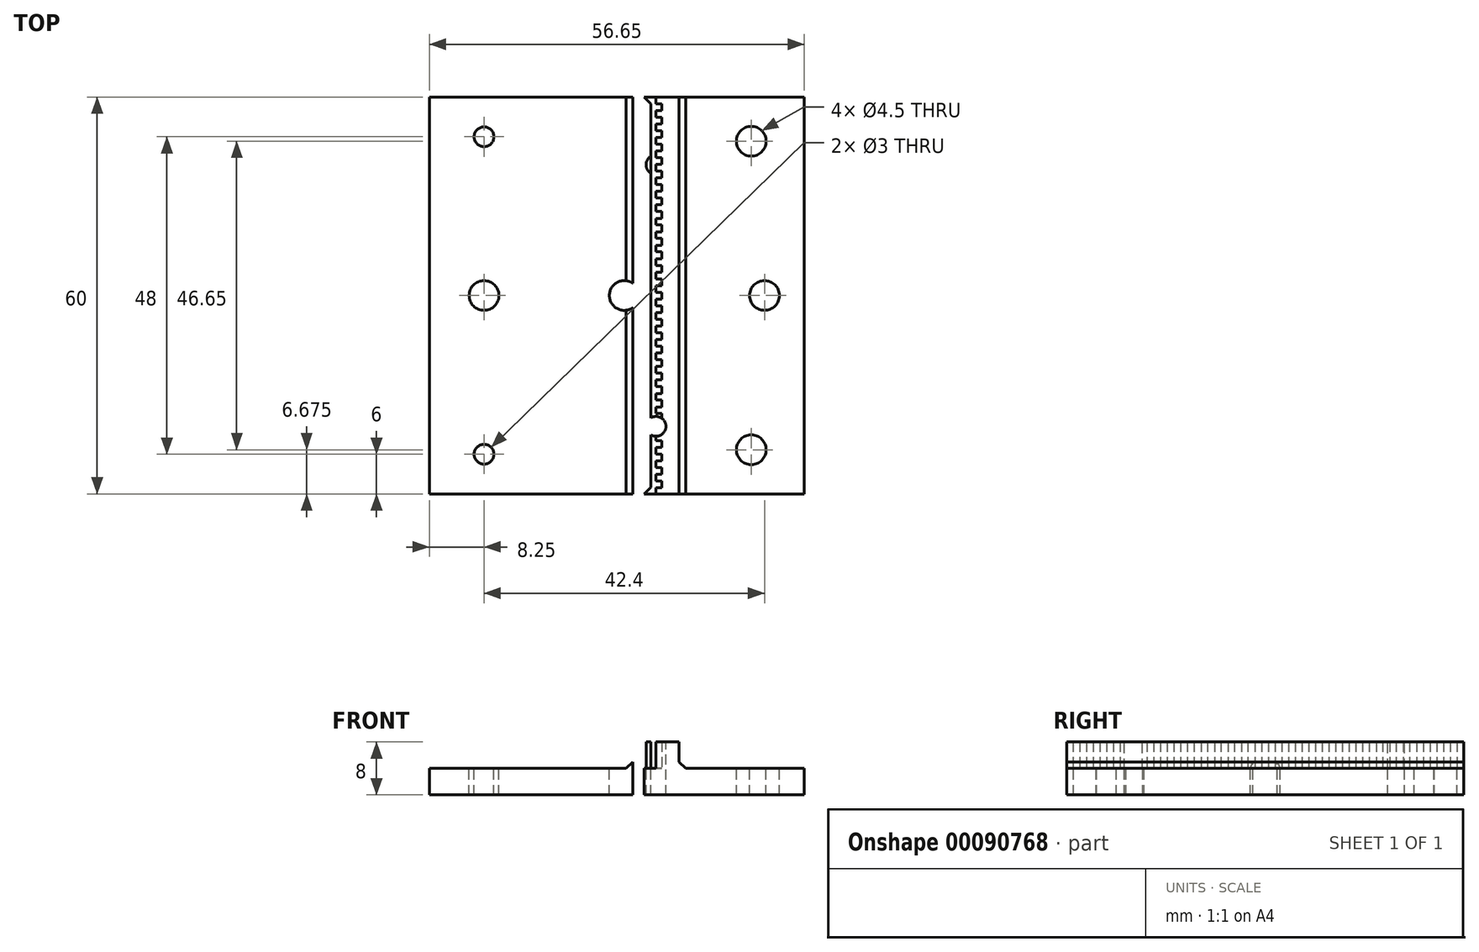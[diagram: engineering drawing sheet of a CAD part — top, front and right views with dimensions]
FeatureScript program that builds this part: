
annotation { "Feature Type Name" : "Feature", "Feature Type Description" : "" }
export const myFeature = defineFeature(function(context is Context, id is Id, definition is map)
    precondition{}
    {
        {
            var Q0;
            Q0=qCreatedBy(makeId("Top.planeOp"),FACE);
            var sketch = newSketch(context, id + "F0", { "sketchPlane" : qUnion([Q0])});
            skLineSegment(sketch, "E0.bottom", {"start": v(28.2, 30) * mm, "end": v(-63.8, 30) * mm});
            skLineSegment(sketch, "E0.top", {"start": v(28.2, -30) * mm, "end": v(-63.8, -30) * mm});
            skLineSegment(sketch, "E0.left", {"start": v(28.2, 30) * mm, "end": v(28.2, -30) * mm});
            skLineSegment(sketch, "E0.right", {"start": v(-63.8, 30) * mm, "end": v(-63.8, -30) * mm});
            skPoint(sketch, "E0.middle", {"position": v(-17.8, 0) * mm});
            skCircle(sketch, "E1.cCircle", {"center": v(6.73, 0) * mm, "radius": 13.47 * mm, "construction": true});
            skLineSegment(sketch, "E1.0", {"start": v(20.2, 23.32) * mm, "end": v(20.2, -23.32) * mm, "construction": true});
            skLineSegment(sketch, "E1.1", {"start": v(20.2, -23.32) * mm, "end": v(-20.2, 0) * mm, "construction": true});
            skLineSegment(sketch, "E1.2", {"start": v(-20.2, 0) * mm, "end": v(20.2, 23.32) * mm, "construction": true});
            skPoint(sketch, "E1.0.midPoint", {"position": v(20.2, 0) * mm});
            skLineSegment(sketch, "E2", {"start": v(-12.7, 30) * mm, "end": v(-12.7, -30) * mm, "construction": true});
            skLineSegment(sketch, "E3", {"start": v(12.7, 30) * mm, "end": v(12.7, -30) * mm, "construction": true});
            skCircle(sketch, "E4", {"center": v(-20.2, 0) * mm, "radius": 2.25 * mm});
            skCircle(sketch, "E5.1.0", {"center": v(20.2, -23.32) * mm, "radius": 2.25 * mm});
            skCircle(sketch, "E5.2.0", {"center": v(20.2, 23.32) * mm, "radius": 2.25 * mm});
            skCircle(sketch, "E6", {"center": v(22.2, 0) * mm, "radius": 2.25 * mm});
            skLineSegment(sketch, "E7.bottom", {"start": v(-33.95, 13) * mm, "end": v(-59.95, 13) * mm, "construction": true});
            skLineSegment(sketch, "E7.top", {"start": v(-33.95, -13) * mm, "end": v(-59.95, -13) * mm, "construction": true});
            skLineSegment(sketch, "E7.left", {"start": v(-33.95, 13) * mm, "end": v(-33.95, -13) * mm, "construction": true});
            skLineSegment(sketch, "E7.right", {"start": v(-59.95, 13) * mm, "end": v(-59.95, -13) * mm, "construction": true});
            skPoint(sketch, "E7.middle", {"position": v(-46.95, 0) * mm});
            skLineSegment(sketch, "E8", {"start": v(-12.7, 0) * mm, "end": v(12.7, 0) * mm, "construction": true});
            skCircle(sketch, "E9", {"center": v(-59.95, 13) * mm, "radius": 1.5 * mm});
            skCircle(sketch, "E10.1.0", {"center": v(-59.95, -13) * mm, "radius": 1.5 * mm});
            skCircle(sketch, "E10.2.0", {"center": v(-33.95, -13) * mm, "radius": 1.5 * mm});
            skCircle(sketch, "E10.3.0", {"center": v(-33.95, 13) * mm, "radius": 1.5 * mm});
            skLineSegment(sketch, "E11.0", {"start": v(-64, 30.2) * mm, "end": v(-64, -30.2) * mm});
            skLineSegment(sketch, "E11.1", {"start": v(28.4, 30.2) * mm, "end": v(-64, 30.2) * mm});
            skLineSegment(sketch, "E11.2", {"start": v(28.4, 30.2) * mm, "end": v(28.4, -30.2) * mm});
            skLineSegment(sketch, "E11.3", {"start": v(28.4, -30.2) * mm, "end": v(-64, -30.2) * mm});
            skLineSegment(sketch, "E12", {"start": v(-28.45, -30.2) * mm, "end": v(-28.45, 30.2) * mm});
            skCircle(sketch, "E13", {"center": v(1, 0) * mm, "radius": 2.25 * mm});
            skCircle(sketch, "E14", {"center": v(-20.2, 24) * mm, "radius": 1.5 * mm});
            skCircle(sketch, "E15.MirrorC", {"center": v(-20.2, -24) * mm, "radius": 1.5 * mm});
            skSolve(sketch);
        }
        {
            var Q0;
            {var subQ0=sQuery(id+"F0.wireOp",EDGE,"E0.left");Q0=makeQuery(id+"F0.imprint","IMPRINT",FACE,{"disambiguationData":[TD([[makeQuery(id+"F0.imprint","IMPRINT",EDGE,{"derivedFrom":subQ0}),-1.0]])]});}
            extrude(context, id + "F1", {"entities" : qUnion([Q0]), "oppositeDirection" : true, "depth" : 1 * mm});
        }
        {
            var Q0;
            {var subQ0=sQuery(id+"F0.wireOp",EDGE,"E0.left");Q0=makeQuery(id+"F0.imprint","IMPRINT",FACE,{"disambiguationData":[TD([[makeQuery(id+"F0.imprint","IMPRINT",EDGE,{"derivedFrom":subQ0}),-1.0]])]});}
            extrude(context, id + "F2", {"entities" : qUnion([Q0]), "operationType" : NewBodyOperationType.ADD, "depth" : 3 * mm});
        }
        {
            var Q0;
            Q0=makeQuery(id+"F2.opExtrude","CAP_FACE",FACE,{"disambiguationData":[OSD([sQuery(id+"F0.wireOp",EDGE,"E0.bottom"),sQuery(id+"F0.wireOp",EDGE,"E0.top"),sQuery(id+"F0.wireOp",EDGE,"E0.left"),sQuery(id+"F0.wireOp",EDGE,"E0.right"),sQuery(id+"F0.wireOp",EDGE,"E4"),sQuery(id+"F0.wireOp",EDGE,"E5.1.0"),sQuery(id+"F0.wireOp",EDGE,"E5.2.0"),sQuery(id+"F0.wireOp",EDGE,"E6"),sQuery(id+"F0.wireOp",EDGE,"E9"),sQuery(id+"F0.wireOp",EDGE,"E10.1.0"),sQuery(id+"F0.wireOp",EDGE,"E10.2.0"),sQuery(id+"F0.wireOp",EDGE,"E10.3.0")])],"isStart":false});
            var sketch = newSketch(context, id + "F3", { "sketchPlane" : qUnion([Q0])});
            skLineSegment(sketch, "E16", {"start": v(5.8, 30) * mm, "end": v(5.8, 29) * mm});
            skLineSegment(sketch, "E17", {"start": v(5.8, 29) * mm, "end": v(6.7, 29) * mm});
            skLineSegment(sketch, "E18", {"start": v(6.7, 29) * mm, "end": v(6.7, 27.96) * mm});
            skLineSegment(sketch, "E19", {"start": v(5.8, 30) * mm, "end": v(6.7, 30) * mm});
            skLineSegment(sketch, "E20.0.1.0", {"start": v(5.8, 27.96) * mm, "end": v(6.7, 27.96) * mm});
            skLineSegment(sketch, "E20.0.1.1", {"start": v(5.8, 27.96) * mm, "end": v(5.8, 26.96) * mm});
            skLineSegment(sketch, "E20.0.1.2", {"start": v(5.8, 26.96) * mm, "end": v(6.7, 26.96) * mm});
            skLineSegment(sketch, "E20.0.1.3", {"start": v(6.7, 26.96) * mm, "end": v(6.7, 25.93) * mm});
            skLineSegment(sketch, "E20.0.2.0", {"start": v(5.8, 25.93) * mm, "end": v(6.7, 25.93) * mm});
            skLineSegment(sketch, "E20.0.2.1", {"start": v(5.8, 25.93) * mm, "end": v(5.8, 24.93) * mm});
            skLineSegment(sketch, "E20.0.2.2", {"start": v(5.8, 24.93) * mm, "end": v(6.7, 24.93) * mm});
            skLineSegment(sketch, "E20.0.2.3", {"start": v(6.7, 24.93) * mm, "end": v(6.7, 23.89) * mm});
            skLineSegment(sketch, "E20.0.3.0", {"start": v(5.8, 23.89) * mm, "end": v(6.7, 23.89) * mm});
            skLineSegment(sketch, "E20.0.3.1", {"start": v(5.8, 23.89) * mm, "end": v(5.8, 22.89) * mm});
            skLineSegment(sketch, "E20.0.3.2", {"start": v(5.8, 22.89) * mm, "end": v(6.7, 22.89) * mm});
            skLineSegment(sketch, "E20.0.3.3", {"start": v(6.7, 22.89) * mm, "end": v(6.7, 21.85) * mm});
            skLineSegment(sketch, "E20.0.4.0", {"start": v(5.8, 21.85) * mm, "end": v(6.7, 21.85) * mm});
            skLineSegment(sketch, "E20.0.4.1", {"start": v(5.8, 21.85) * mm, "end": v(5.8, 20.85) * mm});
            skLineSegment(sketch, "E20.0.4.2", {"start": v(5.8, 20.85) * mm, "end": v(6.7, 20.85) * mm});
            skLineSegment(sketch, "E20.0.4.3", {"start": v(6.7, 20.85) * mm, "end": v(6.7, 19.82) * mm});
            skLineSegment(sketch, "E20.0.5.0", {"start": v(5.8, 19.82) * mm, "end": v(6.7, 19.82) * mm});
            skLineSegment(sketch, "E20.0.5.1", {"start": v(5.8, 19.82) * mm, "end": v(5.8, 18.82) * mm});
            skLineSegment(sketch, "E20.0.5.2", {"start": v(5.8, 18.82) * mm, "end": v(6.7, 18.82) * mm});
            skLineSegment(sketch, "E20.0.5.3", {"start": v(6.7, 18.82) * mm, "end": v(6.7, 17.78) * mm});
            skLineSegment(sketch, "E20.0.6.0", {"start": v(5.8, 17.78) * mm, "end": v(6.7, 17.78) * mm});
            skLineSegment(sketch, "E20.0.6.1", {"start": v(5.8, 17.78) * mm, "end": v(5.8, 16.78) * mm});
            skLineSegment(sketch, "E20.0.6.2", {"start": v(5.8, 16.78) * mm, "end": v(6.7, 16.78) * mm});
            skLineSegment(sketch, "E20.0.6.3", {"start": v(6.7, 16.78) * mm, "end": v(6.7, 15.74) * mm});
            skLineSegment(sketch, "E20.0.7.0", {"start": v(5.8, 15.74) * mm, "end": v(6.7, 15.74) * mm});
            skLineSegment(sketch, "E20.0.7.1", {"start": v(5.8, 15.74) * mm, "end": v(5.8, 14.74) * mm});
            skLineSegment(sketch, "E20.0.7.2", {"start": v(5.8, 14.74) * mm, "end": v(6.7, 14.74) * mm});
            skLineSegment(sketch, "E20.0.7.3", {"start": v(6.7, 14.74) * mm, "end": v(6.7, 13.7) * mm});
            skLineSegment(sketch, "E20.0.8.0", {"start": v(5.8, 13.7) * mm, "end": v(6.7, 13.7) * mm});
            skLineSegment(sketch, "E20.0.8.1", {"start": v(5.8, 13.7) * mm, "end": v(5.8, 12.7) * mm});
            skLineSegment(sketch, "E20.0.8.2", {"start": v(5.8, 12.7) * mm, "end": v(6.7, 12.7) * mm});
            skLineSegment(sketch, "E20.0.8.3", {"start": v(6.7, 12.7) * mm, "end": v(6.7, 11.67) * mm});
            skLineSegment(sketch, "E20.0.9.0", {"start": v(5.8, 11.67) * mm, "end": v(6.7, 11.67) * mm});
            skLineSegment(sketch, "E20.0.9.1", {"start": v(5.8, 11.67) * mm, "end": v(5.8, 10.67) * mm});
            skLineSegment(sketch, "E20.0.9.2", {"start": v(5.8, 10.67) * mm, "end": v(6.7, 10.67) * mm});
            skLineSegment(sketch, "E20.0.9.3", {"start": v(6.7, 10.67) * mm, "end": v(6.7, 9.63) * mm});
            skLineSegment(sketch, "E20.0.10.0", {"start": v(5.8, 9.63) * mm, "end": v(6.7, 9.63) * mm});
            skLineSegment(sketch, "E20.0.10.1", {"start": v(5.8, 9.63) * mm, "end": v(5.8, 8.63) * mm});
            skLineSegment(sketch, "E20.0.10.2", {"start": v(5.8, 8.63) * mm, "end": v(6.7, 8.63) * mm});
            skLineSegment(sketch, "E20.0.10.3", {"start": v(6.7, 8.63) * mm, "end": v(6.7, 7.6) * mm});
            skLineSegment(sketch, "E20.0.11.0", {"start": v(5.8, 7.6) * mm, "end": v(6.7, 7.6) * mm});
            skLineSegment(sketch, "E20.0.11.1", {"start": v(5.8, 7.6) * mm, "end": v(5.8, 6.6) * mm});
            skLineSegment(sketch, "E20.0.11.2", {"start": v(5.8, 6.6) * mm, "end": v(6.7, 6.6) * mm});
            skLineSegment(sketch, "E20.0.11.3", {"start": v(6.7, 6.6) * mm, "end": v(6.7, 5.56) * mm});
            skLineSegment(sketch, "E20.0.12.0", {"start": v(5.8, 5.56) * mm, "end": v(6.7, 5.56) * mm});
            skLineSegment(sketch, "E20.0.12.1", {"start": v(5.8, 5.56) * mm, "end": v(5.8, 4.56) * mm});
            skLineSegment(sketch, "E20.0.12.2", {"start": v(5.8, 4.56) * mm, "end": v(6.7, 4.56) * mm});
            skLineSegment(sketch, "E20.0.12.3", {"start": v(6.7, 4.56) * mm, "end": v(6.7, 3.52) * mm});
            skLineSegment(sketch, "E20.0.13.0", {"start": v(5.8, 3.52) * mm, "end": v(6.7, 3.52) * mm});
            skLineSegment(sketch, "E20.0.13.1", {"start": v(5.8, 3.52) * mm, "end": v(5.8, 2.52) * mm});
            skLineSegment(sketch, "E20.0.13.2", {"start": v(5.8, 2.52) * mm, "end": v(6.7, 2.52) * mm});
            skLineSegment(sketch, "E20.0.13.3", {"start": v(6.7, 2.52) * mm, "end": v(6.7, 1.48) * mm});
            skLineSegment(sketch, "E20.0.14.0", {"start": v(5.8, 1.48) * mm, "end": v(6.7, 1.48) * mm});
            skLineSegment(sketch, "E20.0.14.1", {"start": v(5.8, 1.48) * mm, "end": v(5.8, 0.48) * mm});
            skLineSegment(sketch, "E20.0.14.2", {"start": v(5.8, 0.48) * mm, "end": v(6.7, 0.48) * mm});
            skLineSegment(sketch, "E20.0.14.3", {"start": v(6.7, 0.48) * mm, "end": v(6.7, -0.55) * mm});
            skLineSegment(sketch, "E20.0.15.0", {"start": v(5.8, -0.55) * mm, "end": v(6.7, -0.55) * mm});
            skLineSegment(sketch, "E20.0.15.1", {"start": v(5.8, -0.55) * mm, "end": v(5.8, -1.55) * mm});
            skLineSegment(sketch, "E20.0.15.2", {"start": v(5.8, -1.55) * mm, "end": v(6.7, -1.55) * mm});
            skLineSegment(sketch, "E20.0.15.3", {"start": v(6.7, -1.55) * mm, "end": v(6.7, -2.6) * mm});
            skLineSegment(sketch, "E20.0.16.0", {"start": v(5.8, -2.6) * mm, "end": v(6.7, -2.6) * mm});
            skLineSegment(sketch, "E20.0.16.1", {"start": v(5.8, -2.6) * mm, "end": v(5.8, -3.6) * mm});
            skLineSegment(sketch, "E20.0.16.2", {"start": v(5.8, -3.6) * mm, "end": v(6.7, -3.6) * mm});
            skLineSegment(sketch, "E20.0.16.3", {"start": v(6.7, -3.6) * mm, "end": v(6.7, -4.63) * mm});
            skLineSegment(sketch, "E20.0.17.0", {"start": v(5.8, -4.63) * mm, "end": v(6.7, -4.63) * mm});
            skLineSegment(sketch, "E20.0.17.1", {"start": v(5.8, -4.63) * mm, "end": v(5.8, -5.63) * mm});
            skLineSegment(sketch, "E20.0.17.2", {"start": v(5.8, -5.63) * mm, "end": v(6.7, -5.63) * mm});
            skLineSegment(sketch, "E20.0.17.3", {"start": v(6.7, -5.63) * mm, "end": v(6.7, -6.67) * mm});
            skLineSegment(sketch, "E20.0.18.0", {"start": v(5.8, -6.67) * mm, "end": v(6.7, -6.67) * mm});
            skLineSegment(sketch, "E20.0.18.1", {"start": v(5.8, -6.67) * mm, "end": v(5.8, -7.67) * mm});
            skLineSegment(sketch, "E20.0.18.2", {"start": v(5.8, -7.67) * mm, "end": v(6.7, -7.67) * mm});
            skLineSegment(sketch, "E20.0.18.3", {"start": v(6.7, -7.67) * mm, "end": v(6.7, -8.7) * mm});
            skLineSegment(sketch, "E20.0.19.0", {"start": v(5.8, -8.7) * mm, "end": v(6.7, -8.7) * mm});
            skLineSegment(sketch, "E20.0.19.1", {"start": v(5.8, -8.7) * mm, "end": v(5.8, -9.7) * mm});
            skLineSegment(sketch, "E20.0.19.2", {"start": v(5.8, -9.7) * mm, "end": v(6.7, -9.7) * mm});
            skLineSegment(sketch, "E20.0.19.3", {"start": v(6.7, -9.7) * mm, "end": v(6.7, -10.74) * mm});
            skLineSegment(sketch, "E20.0.20.0", {"start": v(5.8, -10.74) * mm, "end": v(6.7, -10.74) * mm});
            skLineSegment(sketch, "E20.0.20.1", {"start": v(5.8, -10.74) * mm, "end": v(5.8, -11.74) * mm});
            skLineSegment(sketch, "E20.0.20.2", {"start": v(5.8, -11.74) * mm, "end": v(6.7, -11.74) * mm});
            skLineSegment(sketch, "E20.0.20.3", {"start": v(6.7, -11.74) * mm, "end": v(6.7, -12.78) * mm});
            skLineSegment(sketch, "E20.0.21.0", {"start": v(5.8, -12.78) * mm, "end": v(6.7, -12.78) * mm});
            skLineSegment(sketch, "E20.0.21.1", {"start": v(5.8, -12.78) * mm, "end": v(5.8, -13.78) * mm});
            skLineSegment(sketch, "E20.0.21.2", {"start": v(5.8, -13.78) * mm, "end": v(6.7, -13.78) * mm});
            skLineSegment(sketch, "E20.0.21.3", {"start": v(6.7, -13.78) * mm, "end": v(6.7, -14.81) * mm});
            skLineSegment(sketch, "E20.0.22.0", {"start": v(5.8, -14.81) * mm, "end": v(6.7, -14.81) * mm});
            skLineSegment(sketch, "E20.0.22.1", {"start": v(5.8, -14.81) * mm, "end": v(5.8, -15.81) * mm});
            skLineSegment(sketch, "E20.0.22.2", {"start": v(5.8, -15.81) * mm, "end": v(6.7, -15.81) * mm});
            skLineSegment(sketch, "E20.0.22.3", {"start": v(6.7, -15.81) * mm, "end": v(6.7, -16.85) * mm});
            skLineSegment(sketch, "E20.0.23.0", {"start": v(5.8, -16.85) * mm, "end": v(6.7, -16.85) * mm});
            skLineSegment(sketch, "E20.0.23.1", {"start": v(5.8, -16.85) * mm, "end": v(5.8, -17.85) * mm});
            skLineSegment(sketch, "E20.0.23.2", {"start": v(5.8, -17.85) * mm, "end": v(6.7, -17.85) * mm});
            skLineSegment(sketch, "E20.0.23.3", {"start": v(6.7, -17.85) * mm, "end": v(6.7, -18.89) * mm});
            skLineSegment(sketch, "E20.0.24.0", {"start": v(5.8, -18.89) * mm, "end": v(6.7, -18.89) * mm});
            skLineSegment(sketch, "E20.0.24.1", {"start": v(5.8, -18.89) * mm, "end": v(5.8, -19.89) * mm});
            skLineSegment(sketch, "E20.0.24.2", {"start": v(5.8, -19.89) * mm, "end": v(6.7, -19.89) * mm});
            skLineSegment(sketch, "E20.0.24.3", {"start": v(6.7, -19.89) * mm, "end": v(6.7, -20.92) * mm});
            skLineSegment(sketch, "E20.0.25.0", {"start": v(5.8, -20.92) * mm, "end": v(6.7, -20.92) * mm});
            skLineSegment(sketch, "E20.0.25.1", {"start": v(5.8, -20.92) * mm, "end": v(5.8, -21.92) * mm});
            skLineSegment(sketch, "E20.0.25.2", {"start": v(5.8, -21.92) * mm, "end": v(6.7, -21.92) * mm});
            skLineSegment(sketch, "E20.0.25.3", {"start": v(6.7, -21.92) * mm, "end": v(6.7, -22.96) * mm});
            skLineSegment(sketch, "E20.0.26.0", {"start": v(5.8, -22.96) * mm, "end": v(6.7, -22.96) * mm});
            skLineSegment(sketch, "E20.0.26.1", {"start": v(5.8, -22.96) * mm, "end": v(5.8, -23.96) * mm});
            skLineSegment(sketch, "E20.0.26.2", {"start": v(5.8, -23.96) * mm, "end": v(6.7, -23.96) * mm});
            skLineSegment(sketch, "E20.0.26.3", {"start": v(6.7, -23.96) * mm, "end": v(6.7, -25) * mm});
            skLineSegment(sketch, "E20.0.27.0", {"start": v(5.8, -25) * mm, "end": v(6.7, -25) * mm});
            skLineSegment(sketch, "E20.0.27.1", {"start": v(5.8, -25) * mm, "end": v(5.8, -26) * mm});
            skLineSegment(sketch, "E20.0.27.2", {"start": v(5.8, -26) * mm, "end": v(6.7, -26) * mm});
            skLineSegment(sketch, "E20.0.27.3", {"start": v(6.7, -26) * mm, "end": v(6.7, -27.04) * mm});
            skLineSegment(sketch, "E20.0.28.0", {"start": v(5.8, -27.04) * mm, "end": v(6.7, -27.04) * mm});
            skLineSegment(sketch, "E20.0.28.1", {"start": v(5.8, -27.04) * mm, "end": v(5.8, -28.04) * mm});
            skLineSegment(sketch, "E20.0.28.2", {"start": v(5.8, -28.04) * mm, "end": v(6.7, -28.04) * mm});
            skLineSegment(sketch, "E20.0.28.3", {"start": v(6.7, -28.04) * mm, "end": v(6.7, -29.07) * mm});
            skLineSegment(sketch, "E20.direction1", {"start": v(5.8, 30) * mm, "end": v(27.82, 30) * mm, "construction": true});
            skLineSegment(sketch, "E20.direction2", {"start": v(5.8, 30) * mm, "end": v(5.8, 27.96) * mm, "construction": true});
            skLineSegment(sketch, "E21.0.0.29", {"start": v(5.8, -29.07) * mm, "end": v(6.7, -29.07) * mm});
            skLineSegment(sketch, "E21.3.0.29", {"start": v(5.8, -29.07) * mm, "end": v(5.8, -30.07) * mm});
            skLineSegment(sketch, "E21.6.0.29", {"start": v(5.8, -30.07) * mm, "end": v(6.7, -30.07) * mm});
            skLineSegment(sketch, "E21.9.0.29", {"start": v(6.7, -30.07) * mm, "end": v(6.7, -31.1) * mm});
            skLineSegment(sketch, "E22", {"start": v(2.3, 30) * mm, "end": v(2.3, -30) * mm});
            skLineSegment(sketch, "E23", {"start": v(9.3, -30) * mm, "end": v(9.3, 30) * mm});
            skLineSegment(sketch, "E24", {"start": v(5, -30) * mm, "end": v(5, 30) * mm});
            skSolve(sketch);
        }
        {
            var Q0;
            {var subQ0=sQuery(id+"F3.wireOp",EDGE,"E22");Q0=makeQuery(id+"F3.imprint","IMPRINT",FACE,{"disambiguationData":[TD([[makeQuery(id+"F3.imprint","IMPRINT",EDGE,{"derivedFrom":subQ0}),1.0]])]});}
            var Q1;
            Q1=makeQuery(id+"F3.imprint","IMPRINT",FACE,{"disambiguationData":[TD([[makeQuery(id+"F3.imprint","IMPRINT",EDGE,{"derivedFrom":sQuery(id+"F3.wireOp",EDGE,"E16")}),1.0]])]});
            extrude(context, id + "F4", {"entities" : qUnion([Q0, Q1]), "operationType" : NewBodyOperationType.ADD, "depth" : 4 * mm});
        }
        {
            var Q0;
            Q0=makeQuery(id+"F4.opExtrude","CAP_EDGE",EDGE,{"disambiguationData":[OSD([sQuery(id+"F3.wireOp",EDGE,"E22")])],"isStart":true});
            var Q1;
            Q1=makeQuery(id+"F4.opExtrude","CAP_EDGE",EDGE,{"disambiguationData":[OSD([sQuery(id+"F3.wireOp",EDGE,"E23")])],"isStart":true});
            var Q2;
            Q2=makeQuery(id+"F4.opExtrude","SWEPT_EDGE",EDGE,{"disambiguationData":[OSD([sQuery(id+"F0.wireOp",EDGE,"E0.top"),sQuery(id+"F3.wireOp",EDGE,"E24")])]});
            var Q3;
            Q3=makeQuery(id+"F4.opExtrude","SWEPT_EDGE",EDGE,{"disambiguationData":[OSD([sQuery(id+"F0.wireOp",EDGE,"E0.bottom"),sQuery(id+"F3.wireOp",EDGE,"E24")])]});
            chamfer(context, id + "F5", {"entities" : qUnion([Q0, Q1, Q2, Q3]), "width" : 1 * mm, "tangentPropagation" : true});
        }
        {
            var Q0;
            Q0=makeQuery(id+"F4.opExtrude","CAP_FACE",FACE,{"disambiguationData":[OSD([sQuery(id+"F0.wireOp",EDGE,"E0.bottom"),sQuery(id+"F0.wireOp",EDGE,"E0.top"),sQuery(id+"F3.wireOp",EDGE,"E22"),sQuery(id+"F3.wireOp",EDGE,"E24")])],"isStart":false});
            var sketch = newSketch(context, id + "F6", { "sketchPlane" : qUnion([Q0])});
            skLineSegment(sketch, "E25", {"start": v(2.3, 0) * mm, "end": v(9.3, 0) * mm, "construction": true});
            skCircle(sketch, "E26", {"center": v(5.8, -19.78) * mm, "radius": 1.5 * mm});
            skLineSegment(sketch, "E27.0", {"start": v(9.3, -30) * mm, "end": v(9.3, 30) * mm});
            skPoint(sketch, "E28", {"position": v(5.8, 0) * mm});
            skCircle(sketch, "E29.MirrorC", {"center": v(5.8, 19.78) * mm, "radius": 1.5 * mm});
            skSolve(sketch);
        }
        {
            var Q0;
            {var subQ0=sQuery(id+"F6.wireOp",EDGE,"E26");var subQ1=makeQuery(id+"F4.opExtrude","CAP_EDGE",EDGE,{"disambiguationData":[OSD([sQuery(id+"F3.wireOp",EDGE,"E24")])],"isStart":false});var subQ2=makeQuery(id+"F6.imprint","INTERSECT",VERTEX,{"disambiguationData":[OD(0.0)],"derivedFrom":[subQ1,subQ0]});Q0=makeQuery(id+"F6.imprint","IMPRINT",FACE,{"disambiguationData":[TD([[makeQuery(id+"F6.imprint","IMPRINT",EDGE,{"disambiguationData":[TD([[subQ2,-1.0]])],"derivedFrom":subQ0}),1.0]])]});}
            var Q1;
            {var subQ0=sQuery(id+"F6.wireOp",EDGE,"E26");var subQ1=makeQuery(id+"F4.opExtrude","CAP_EDGE",EDGE,{"disambiguationData":[OSD([sQuery(id+"F3.wireOp",EDGE,"E24")])],"isStart":false});var subQ2=makeQuery(id+"F6.imprint","INTERSECT",VERTEX,{"disambiguationData":[OD(0.0)],"derivedFrom":[subQ1,subQ0]});Q1=makeQuery(id+"F6.imprint","IMPRINT",FACE,{"disambiguationData":[TD([[makeQuery(id+"F6.imprint","IMPRINT",EDGE,{"disambiguationData":[TD([[subQ2,1.0]])],"derivedFrom":subQ0}),1.0]])]});}
            var Q2;
            {var subQ0=sQuery(id+"F6.wireOp",EDGE,"E29.MirrorC");var subQ1=makeQuery(id+"F4.opExtrude","CAP_EDGE",EDGE,{"disambiguationData":[OSD([sQuery(id+"F3.wireOp",EDGE,"E24")])],"isStart":false});var subQ2=makeQuery(id+"F6.imprint","INTERSECT",VERTEX,{"disambiguationData":[OD(0.0)],"derivedFrom":[subQ1,subQ0]});Q2=makeQuery(id+"F6.imprint","IMPRINT",FACE,{"disambiguationData":[TD([[makeQuery(id+"F6.imprint","IMPRINT",EDGE,{"disambiguationData":[TD([[subQ2,1.0]])],"derivedFrom":subQ0}),-1.0]])]});}
            var Q3;
            {var subQ0=sQuery(id+"F6.wireOp",EDGE,"E29.MirrorC");var subQ1=makeQuery(id+"F4.opExtrude","CAP_EDGE",EDGE,{"disambiguationData":[OSD([sQuery(id+"F3.wireOp",EDGE,"E24")])],"isStart":false});var subQ2=makeQuery(id+"F6.imprint","INTERSECT",VERTEX,{"disambiguationData":[OD(0.0)],"derivedFrom":[subQ1,subQ0]});Q3=makeQuery(id+"F6.imprint","IMPRINT",FACE,{"disambiguationData":[TD([[makeQuery(id+"F6.imprint","IMPRINT",EDGE,{"disambiguationData":[TD([[subQ2,-1.0]])],"derivedFrom":subQ0}),-1.0]])]});}
            extrude(context, id + "F7", {"entities" : qUnion([Q0, Q1, Q2, Q3]), "operationType" : NewBodyOperationType.REMOVE, "oppositeDirection" : true, "depth" : 25 * mm});
        }
    });
